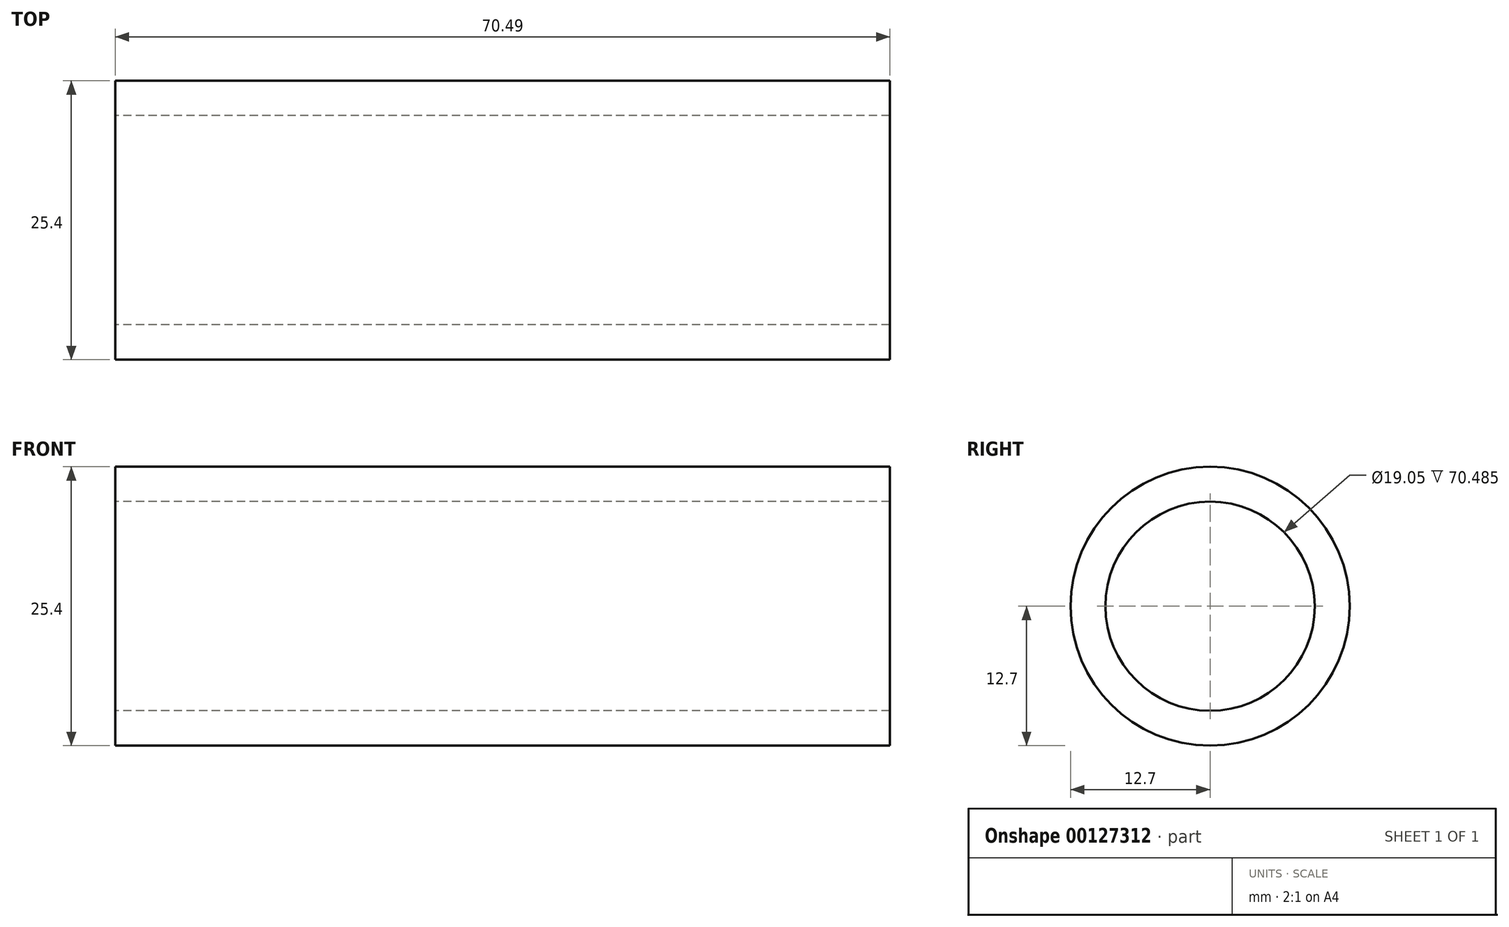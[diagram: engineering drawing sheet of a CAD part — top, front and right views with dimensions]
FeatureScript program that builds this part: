
annotation { "Feature Type Name" : "Feature", "Feature Type Description" : "" }
export const myFeature = defineFeature(function(context is Context, id is Id, definition is map)
    precondition{}
    {
        {
            var Q0;
            Q0=qCreatedBy(makeId("Right.planeOp"),FACE);
            var sketch = newSketch(context, id + "F0", { "sketchPlane" : qUnion([Q0])});
            skCircle(sketch, "E0", {"center": v(0, 0) * mm, "radius": 12.7 * mm});
            skCircle(sketch, "E1", {"center": v(0, 0) * mm, "radius": 9.53 * mm});
            skSolve(sketch);
        }
        {
            var Q0;
            Q0 = qSketchRegion(id + "F0", true);
            extrude(context, id + "F1", {"entities" : qUnion([Q0]), "depth" : 70.48 * mm});
        }
    });
